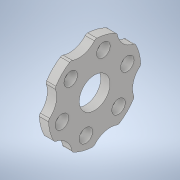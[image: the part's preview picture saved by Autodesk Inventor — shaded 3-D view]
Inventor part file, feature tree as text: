
AUTODESK INVENTOR PART (.ipt)
format: ipt  version: 2021 (Build 250183000, 183)  size: 174,080 bytes
history: native  units: in
note: dims shown in document units (in); Inventor stores cm internally (conversion verified against a paired STEP export)
features: extrude x1, fillet x1, sketch x1
ambient origin geometry x8: Origin, YZ Plane, XZ Plane, XY Plane, X Axis, Y Axis, Z Axis, Center Point
bodies: Solid1 (feature_tree)
feature tree (3):
  extrude  "Extrusion1"  Depth=0.125in
  fillet  "Fillet1"  Radius=0.55in
  sketch  "Sketch1"  dims[d0=3.75in d1=2.75in d2=0.55in d3=45.0deg d4=2.3622in d6=360.0deg d8=1.25in d12=1.65in d16=15.0deg d17=2.3622in d19=360.0deg d21=0.375in d22=0.0in d23=0.125in]
